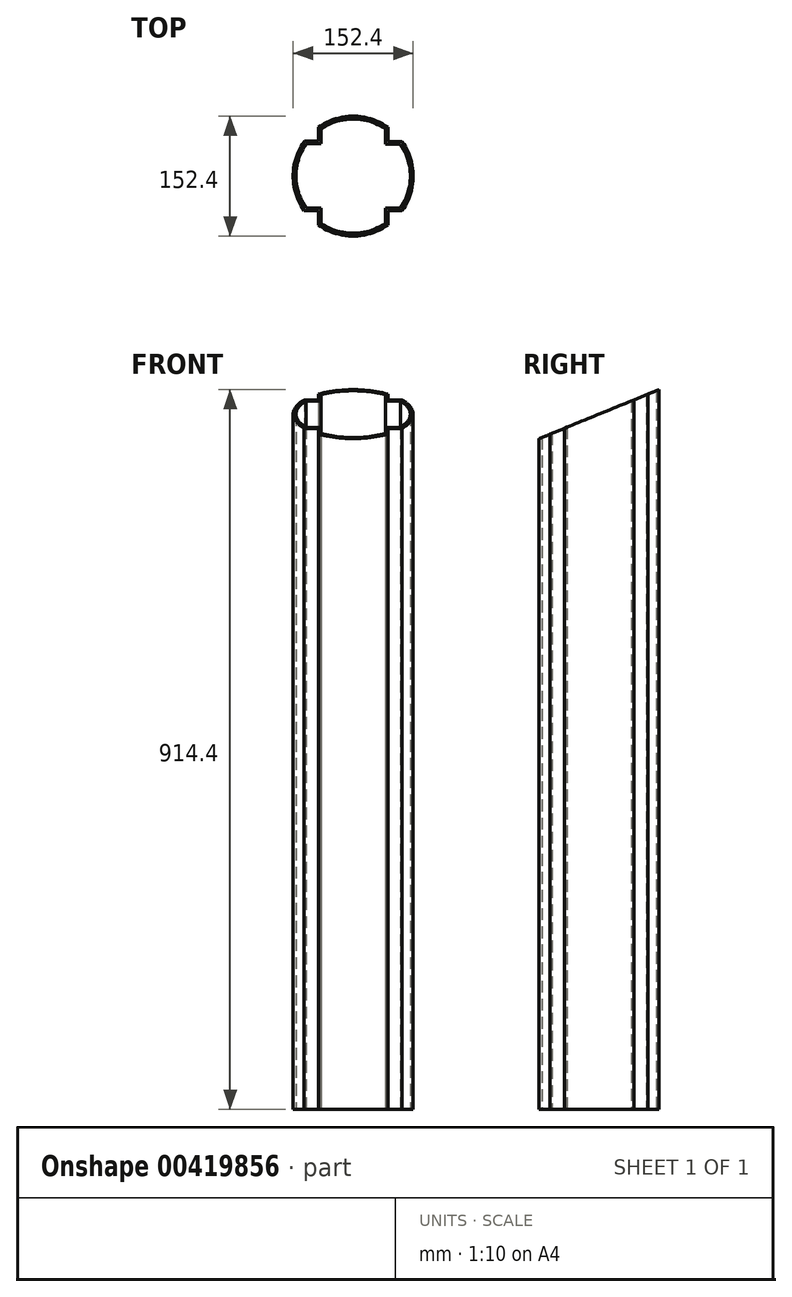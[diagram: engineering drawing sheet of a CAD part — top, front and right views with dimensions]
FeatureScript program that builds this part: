
annotation { "Feature Type Name" : "Feature", "Feature Type Description" : "" }
export const myFeature = defineFeature(function(context is Context, id is Id, definition is map)
    precondition{}
    {
        {
            var Q0;
            Q0=qCreatedBy(makeId("Top.planeOp"),FACE);
            var sketch = newSketch(context, id + "F0", { "sketchPlane" : qUnion([Q0])});
            skArc(sketch, "E0", {"start": v(-62.06, 44.21) * mm, "mid": v(-76.2, 0.05) * mm, "end": v(-62.12, -44.13) * mm});
            skArc(sketch, "E1.0", {"start": v(-59.95, 41.03) * mm, "mid": v(-72.64, 0.05) * mm, "end": v(-60, -40.95) * mm});
            skLineSegment(sketch, "E2", {"start": v(-44.07, 44.19) * mm, "end": v(-44.04, 62.18) * mm});
            skLineSegment(sketch, "E3", {"start": v(-62.12, -44.13) * mm, "end": v(-44.13, -44.13) * mm});
            skLineSegment(sketch, "E4", {"start": v(-44.13, -44.13) * mm, "end": v(-44.13, -62.12) * mm});
            skLineSegment(sketch, "E5", {"start": v(44.13, 62.12) * mm, "end": v(44.13, 44.13) * mm});
            skLineSegment(sketch, "E6", {"start": v(44.13, 44.13) * mm, "end": v(62.12, 44.13) * mm});
            skLineSegment(sketch, "E7", {"start": v(44.13, -62.12) * mm, "end": v(44.13, -44.13) * mm});
            skLineSegment(sketch, "E8", {"start": v(44.13, -44.13) * mm, "end": v(62.12, -44.13) * mm});
            skLineSegment(sketch, "E9", {"start": v(-44.07, 44.19) * mm, "end": v(-62.06, 44.21) * mm});
            skArc(sketch, "E10.trimOffspring", {"start": v(44.13, 62.12) * mm, "mid": v(0.05, 76.2) * mm, "end": v(-44.04, 62.18) * mm});
            skArc(sketch, "E11.trimOffspring", {"start": v(40.95, 60) * mm, "mid": v(0.05, 72.64) * mm, "end": v(-40.87, 60.06) * mm});
            skArc(sketch, "E12.trimOffspring", {"start": v(-40.95, -60) * mm, "mid": v(0, -72.64) * mm, "end": v(40.95, -60) * mm});
            skArc(sketch, "E13.trimOffspring", {"start": v(-44.13, -62.12) * mm, "mid": v(0, -76.2) * mm, "end": v(44.13, -62.12) * mm});
            skArc(sketch, "E14.trimOffspring", {"start": v(60, -40.95) * mm, "mid": v(72.64, 0) * mm, "end": v(60, 40.95) * mm});
            skArc(sketch, "E15.trimOffspring", {"start": v(62.12, -44.13) * mm, "mid": v(76.2, 0) * mm, "end": v(62.12, 44.13) * mm});
            skLineSegment(sketch, "E16", {"start": v(-59.95, 41.03) * mm, "end": v(-40.9, 41) * mm});
            skLineSegment(sketch, "E17", {"start": v(-40.9, 41) * mm, "end": v(-40.87, 60.06) * mm});
            skLineSegment(sketch, "E18", {"start": v(40.95, 60) * mm, "end": v(40.95, 40.95) * mm});
            skLineSegment(sketch, "E19", {"start": v(40.95, 40.95) * mm, "end": v(60, 40.95) * mm});
            skLineSegment(sketch, "E20", {"start": v(-60, -40.95) * mm, "end": v(-40.95, -40.95) * mm});
            skLineSegment(sketch, "E21", {"start": v(-40.95, -40.95) * mm, "end": v(-40.95, -60) * mm});
            skLineSegment(sketch, "E22", {"start": v(40.95, -60) * mm, "end": v(40.95, -40.95) * mm});
            skLineSegment(sketch, "E23", {"start": v(40.95, -40.95) * mm, "end": v(60, -40.95) * mm});
            skPoint(sketch, "E24.end.orphan", {"position": v(62.12, -40.95) * mm});
            skSolve(sketch);
        }
        {
            var Q0;
            Q0 = qSketchRegion(id + "F0", true);
            extrude(context, id + "F1", {"entities" : qUnion([Q0]), "depth" : 914.4 * mm});
        }
        {
            var Q0;
            Q0=qCreatedBy(makeId("Right.planeOp"),FACE);
            var sketch = newSketch(context, id + "F2", { "sketchPlane" : qUnion([Q0])});
            skLineSegment(sketch, "E25.bottom", {"start": v(76.2, 914.4) * mm, "end": v(-76.2, 914.4) * mm});
            skLineSegment(sketch, "E25.right", {"start": v(-76.2, 914.4) * mm, "end": v(-76.2, 852.05) * mm});
            skPoint(sketch, "E25.middle", {"position": v(0, 883.23) * mm});
            skLineSegment(sketch, "E26", {"start": v(-76.2, 852.05) * mm, "end": v(76.2, 914.4) * mm});
            skPoint(sketch, "E25.left.end.orphan", {"position": v(76.2, 852.05) * mm});
            skSolve(sketch);
        }
        {
            var Q0;
            Q0 = qSketchRegion(id + "F2", true);
            extrude(context, id + "F3", {"entities" : qUnion([Q0]), "operationType" : NewBodyOperationType.REMOVE, "endBound" : BoundingType.THROUGH_ALL, "oppositeDirection" : true, "depth" : 25.4 * mm, "hasSecondDirection" : true, "secondDirectionBound" : SecondDirectionBoundingType.THROUGH_ALL, "secondDirectionOppositeDirection" : false, "secondDirectionDepth" : 25.4 * mm});
        }
    });
